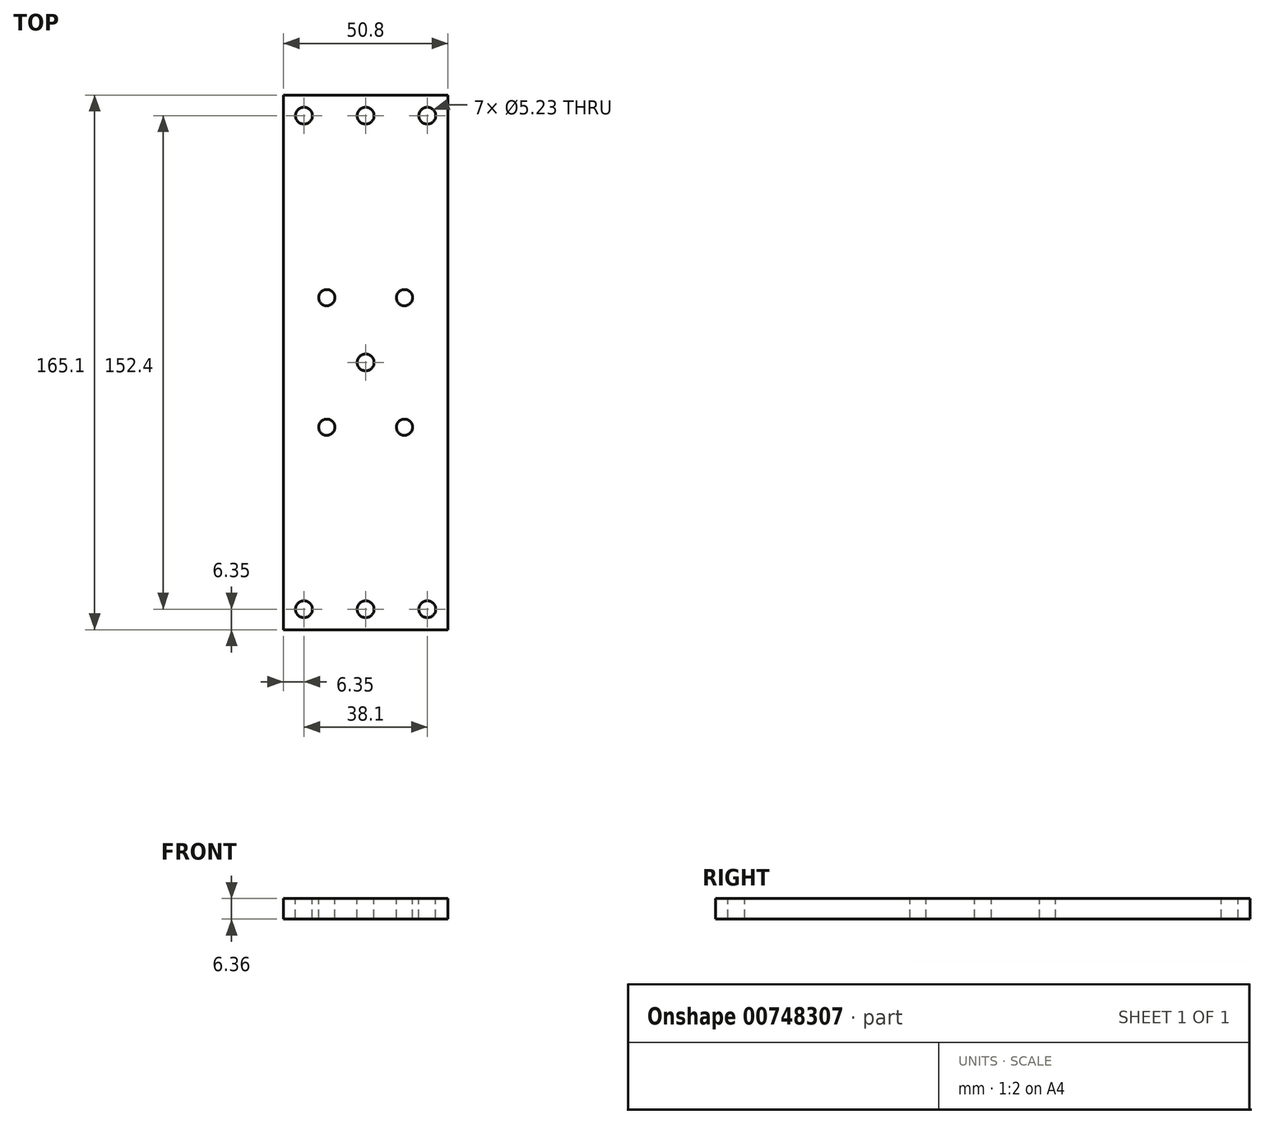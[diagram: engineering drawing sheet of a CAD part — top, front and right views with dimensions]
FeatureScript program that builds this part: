
annotation { "Feature Type Name" : "Feature", "Feature Type Description" : "" }
export const myFeature = defineFeature(function(context is Context, id is Id, definition is map)
    precondition{}
    {
        {
            var Q0;
            Q0=qCreatedBy(makeId("Front.planeOp"),FACE);
            var sketch = newSketch(context, id + "F0", { "sketchPlane" : qUnion([Q0])});
            skLineSegment(sketch, "E0.bottom", {"start": v(25.4, 3.18) * mm, "end": v(-25.4, 3.18) * mm});
            skLineSegment(sketch, "E0.top", {"start": v(25.4, -3.17) * mm, "end": v(-25.4, -3.17) * mm});
            skLineSegment(sketch, "E0.left", {"start": v(25.4, 3.18) * mm, "end": v(25.4, -3.17) * mm});
            skLineSegment(sketch, "E0.right", {"start": v(-25.4, 3.18) * mm, "end": v(-25.4, -3.17) * mm});
            skPoint(sketch, "E0.middle", {"position": v(0, 0) * mm});
            skSolve(sketch);
        }
        {
            var Q0;
            Q0=qSketchRegion(id+"F0",true);
            extrude(context, id + "F1", {"entities" : qUnion([Q0]), "depth" : 165.1 * mm, "offsetDistance" : 25.4 * mm});
        }
        {
            var Q0;
            Q0=makeQuery(id+"F1.opExtrude","SWEPT_FACE",FACE,{"disambiguationData":[OSD([sQuery(id+"F0.wireOp",EDGE,"E0.bottom")])]});
            var sketch = newSketch(context, id + "F2", { "sketchPlane" : qUnion([Q0])});
            skLineSegment(sketch, "E1", {"start": v(-25.4, -82.55) * mm, "end": v(25.4, -82.55) * mm, "construction": true});
            skLineSegment(sketch, "E2", {"start": v(0, -165.1) * mm, "end": v(0, 0) * mm, "construction": true});
            skLineSegment(sketch, "E3.bottom", {"start": v(12, -62.55) * mm, "end": v(-12, -62.55) * mm, "construction": true});
            skLineSegment(sketch, "E3.top", {"start": v(12, -102.55) * mm, "end": v(-12, -102.55) * mm, "construction": true});
            skLineSegment(sketch, "E3.left", {"start": v(12, -62.55) * mm, "end": v(12, -102.55) * mm, "construction": true});
            skLineSegment(sketch, "E3.right", {"start": v(-12, -62.55) * mm, "end": v(-12, -102.55) * mm, "construction": true});
            skPoint(sketch, "E3.middle", {"position": v(0, -82.55) * mm});
            skLineSegment(sketch, "E4", {"start": v(-25.4, -158.75) * mm, "end": v(25.4, -158.75) * mm, "construction": true});
            skLineSegment(sketch, "E5", {"start": v(-25.4, -6.35) * mm, "end": v(25.4, -6.35) * mm, "construction": true});
            skCircle(sketch, "E6", {"center": v(0, -158.75) * mm, "radius": 2.62 * mm});
            skCircle(sketch, "E7", {"center": v(0, -6.35) * mm, "radius": 2.62 * mm});
            skCircle(sketch, "E8", {"center": v(-12, -102.55) * mm, "radius": 2.5 * mm});
            skCircle(sketch, "E9", {"center": v(12, -102.55) * mm, "radius": 2.5 * mm});
            skCircle(sketch, "E10", {"center": v(12, -62.55) * mm, "radius": 2.5 * mm});
            skCircle(sketch, "E11", {"center": v(-12, -62.55) * mm, "radius": 2.5 * mm});
            skCircle(sketch, "E12", {"center": v(0, -82.55) * mm, "radius": 2.62 * mm});
            skLineSegment(sketch, "E13.0", {"start": v(19.05, -165.1) * mm, "end": v(19.05, 0) * mm, "construction": true});
            skLineSegment(sketch, "E14.0", {"start": v(-19.05, -165.1) * mm, "end": v(-19.05, 0) * mm, "construction": true});
            skCircle(sketch, "E15", {"center": v(-19.05, -158.75) * mm, "radius": 2.62 * mm});
            skCircle(sketch, "E16", {"center": v(19.05, -158.75) * mm, "radius": 2.62 * mm});
            skCircle(sketch, "E17", {"center": v(-19.05, -6.35) * mm, "radius": 2.62 * mm});
            skCircle(sketch, "E18", {"center": v(19.05, -6.35) * mm, "radius": 2.62 * mm});
            skSolve(sketch);
        }
        {
            var Q0;
            Q0 = qSketchRegion(id + "F2", true);
            extrude(context, id + "F3", {"entities" : qUnion([Q0]), "operationType" : NewBodyOperationType.REMOVE, "endBound" : BoundingType.THROUGH_ALL, "oppositeDirection" : true, "depth" : 25.4 * mm, "offsetDistance" : 25.4 * mm});
        }
    });
